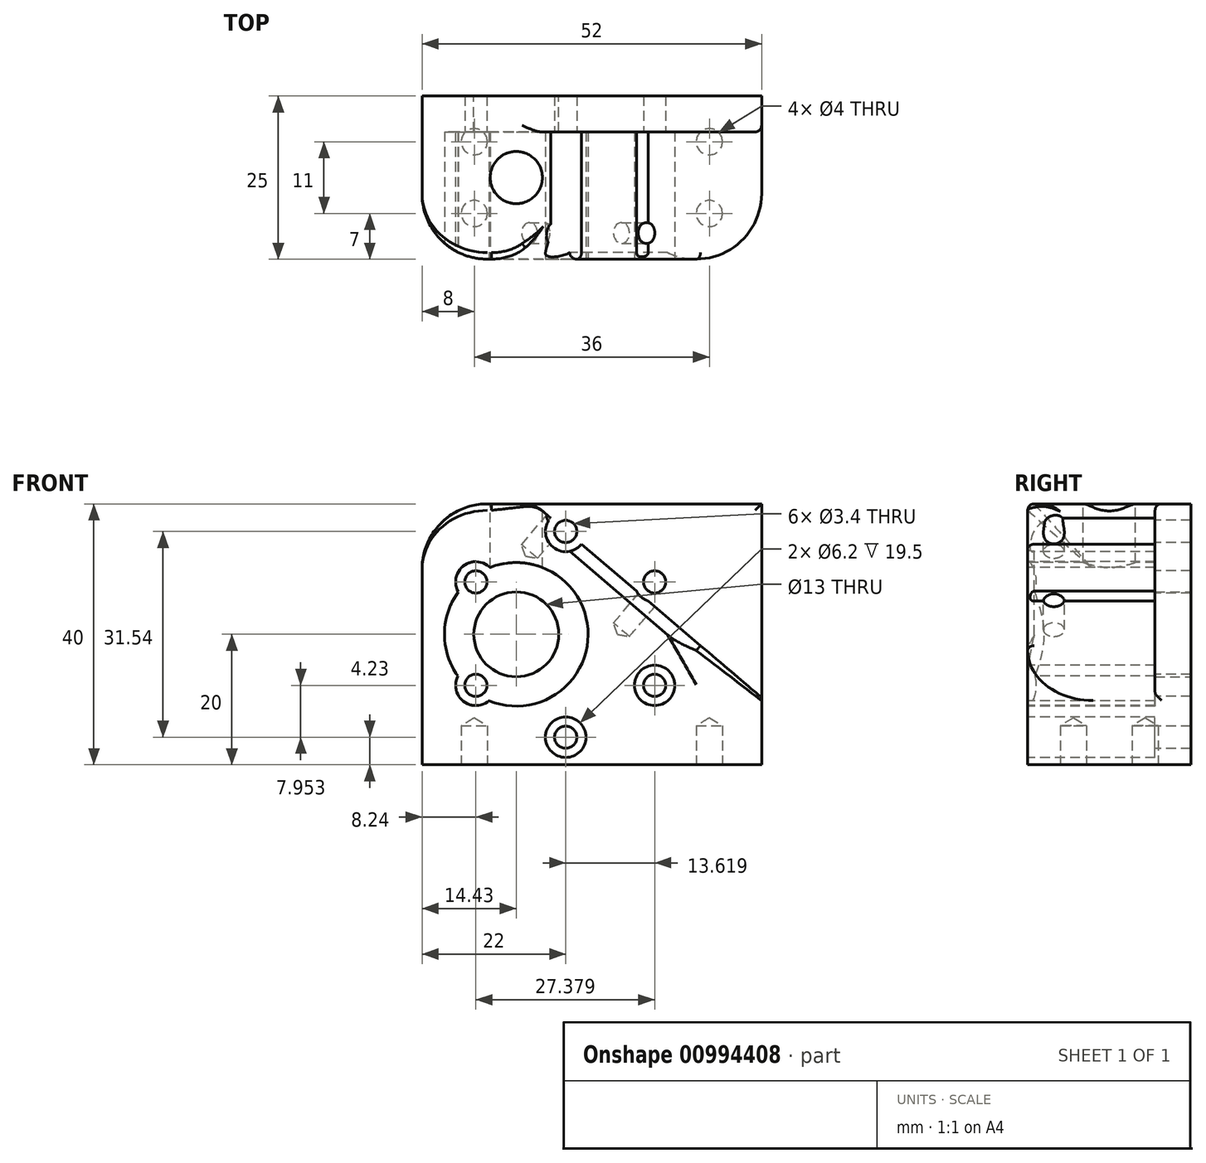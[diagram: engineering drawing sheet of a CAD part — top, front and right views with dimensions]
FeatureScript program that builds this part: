
annotation { "Feature Type Name" : "Feature", "Feature Type Description" : "" }
export const myFeature = defineFeature(function(context is Context, id is Id, definition is map)
    precondition{}
    {
        {
            var Q0;
            Q0=qCreatedBy(makeId("Front.planeOp"),FACE);
            var sketch = newSketch(context, id + "F0", { "sketchPlane" : qUnion([Q0])});
            skLineSegment(sketch, "E0.bottom", {"start": v(26, 20) * mm, "end": v(-26, 20) * mm});
            skLineSegment(sketch, "E0.top", {"start": v(26, -20) * mm, "end": v(-26, -20) * mm});
            skLineSegment(sketch, "E0.left", {"start": v(26, 20) * mm, "end": v(26, -20) * mm});
            skLineSegment(sketch, "E0.right", {"start": v(-26, 20) * mm, "end": v(-26, -20) * mm});
            skPoint(sketch, "E0.middle", {"position": v(0, 0) * mm});
            skLineSegment(sketch, "E1", {"start": v(-4, -15.77) * mm, "end": v(-4, 15.77) * mm});
            skPoint(sketch, "E2", {"position": v(9.66, -7.88) * mm});
            skPoint(sketch, "E3", {"position": v(9.66, 7.88) * mm});
            skPoint(sketch, "E4", {"position": v(11.77, 0) * mm});
            skPoint(sketch, "E5", {"position": v(-17.66, -7.88) * mm});
            skPoint(sketch, "E6", {"position": v(-17.66, 7.88) * mm});
            skCircle(sketch, "E7", {"center": v(-11.57, 0) * mm, "radius": 6.5 * mm});
            skPoint(sketch, "E8.center.orphan", {"position": v(-4, 0) * mm});
            skSolve(sketch);
        }
        {
            var Q0;
            Q0 = qSketchRegion(id + "F0", true);
            extrude(context, id + "F1", {"entities" : qUnion([Q0]), "endBound" : BoundingType.SYMMETRIC, "depth" : 25 * mm, "offsetDistance" : 25 * mm});
        }
        {
            var Q0;
            Q0=makeQuery(id+"F1.opExtrude","CAP_FACE",FACE,{"disambiguationData":[OSD([sQuery(id+"F0.wireOp",EDGE,"E0.bottom"),sQuery(id+"F0.wireOp",EDGE,"E0.top"),sQuery(id+"F0.wireOp",EDGE,"E0.left"),sQuery(id+"F0.wireOp",EDGE,"E0.right"),sQuery(id+"F0.wireOp",EDGE,"E7")])],"isStart":false});
            var sketch = newSketch(context, id + "F2", { "sketchPlane" : qUnion([Q0])});
            skPoint(sketch, "E9", {"position": v(-17.76, -7.82) * mm});
            skPoint(sketch, "E10", {"position": v(-17.76, 8.03) * mm});
            skPoint(sketch, "E11", {"position": v(9.62, -7.82) * mm});
            skPoint(sketch, "E12", {"position": v(9.62, 8.03) * mm});
            skPoint(sketch, "E13", {"position": v(-4, -15.77) * mm});
            skPoint(sketch, "E14", {"position": v(-4, 15.77) * mm});
            skSolve(sketch);
        }
        {
            var Q0;
            Q0=sQuery(id+"F2.wireOp",VERTEX,"E10");
            var Q1;
            Q1=sQuery(id+"F2.wireOp",VERTEX,"E14");
            var Q2;
            Q2=sQuery(id+"F2.wireOp",VERTEX,"E12");
            var Q3;
            Q3=sQuery(id+"F2.wireOp",VERTEX,"E11");
            var Q4;
            Q4=sQuery(id+"F2.wireOp",VERTEX,"E13");
            var Q5;
            Q5=sQuery(id+"F2.wireOp",VERTEX,"E9");
            var Q6;
            Q6=makeQuery(id+"F1.opExtrude","SWEPT_BODY",BODY,{"disambiguationData":[OSD([sQuery(id+"F0.wireOp",EDGE,"E0.bottom"),sQuery(id+"F0.wireOp",EDGE,"E0.top"),sQuery(id+"F0.wireOp",EDGE,"E0.left"),sQuery(id+"F0.wireOp",EDGE,"E0.right"),sQuery(id+"F0.wireOp",EDGE,"E7")])]});
            hole(context, id + "F3", {"style" : HoleStyle.C_BORE, "endStyle" : HoleEndStyle.THROUGH, "holeDiameter" : 3.4 * mm, "cBoreDiameter" : 6.2 * mm, "cBoreDepth" : 19.5 * mm, "majorDiameter" : 3 * mm, "isTappedThrough" : true, "tappedDepth" : 12 * mm, "tapClearance" : 3, "startFromSketch" : true, "locations" : qUnion([Q0, Q1, Q2, Q3, Q4, Q5]), "scope" : qUnion([Q6])});
        }
        {
            var Q0;
            Q0=makeQuery(id+"F2.imprint","IMPRINT",FACE,{"disambiguationData":[TD([[makeQuery(id+"F2.imprint","IMPRINT",EDGE,{"derivedFrom":makeQuery(id+"F1.opExtrude","CAP_EDGE",EDGE,{"disambiguationData":[OSD([sQuery(id+"F0.wireOp",EDGE,"E0.bottom")])],"isStart":false})}),1.0]])]});
            var sketch = newSketch(context, id + "F4", { "sketchPlane" : qUnion([Q0])});
            skCircle(sketch, "E15", {"center": v(-11.57, 0) * mm, "radius": 11 * mm});
            skSolve(sketch);
        }
        {
            var Q0;
            Q0 = qSketchRegion(id + "F4", true);
            extrude(context, id + "F5", {"entities" : qUnion([Q0]), "operationType" : NewBodyOperationType.REMOVE, "oppositeDirection" : true, "depth" : 19.5 * mm, "offsetDistance" : 25 * mm});
        }
        {
            var Q0;
            Q0=makeQuery(id+"F1.opExtrude","SWEPT_FACE",FACE,{"disambiguationData":[OSD([sQuery(id+"F0.wireOp",EDGE,"E0.bottom")])]});
            var sketch = newSketch(context, id + "F6", { "sketchPlane" : qUnion([Q0])});
            skPoint(sketch, "E16", {"position": v(-17.67, 0) * mm});
            skPoint(sketch, "E17", {"position": v(36.59, -1463.42) * mm});
            skPoint(sketch, "E18", {"position": v(-11.57, 0) * mm});
            skSolve(sketch);
        }
        {
            var Q0;
            Q0=sQuery(id+"F6.wireOp",VERTEX,"E18");
            var Q1;
            Q1=makeQuery(id+"F1.opExtrude","SWEPT_BODY",BODY,{"disambiguationData":[OSD([sQuery(id+"F0.wireOp",EDGE,"E0.bottom"),sQuery(id+"F0.wireOp",EDGE,"E0.top"),sQuery(id+"F0.wireOp",EDGE,"E0.left"),sQuery(id+"F0.wireOp",EDGE,"E0.right"),sQuery(id+"F0.wireOp",EDGE,"E7")])]});
            hole(context, id + "F7", {"style" : HoleStyle.SIMPLE, "endStyle" : HoleEndStyle.BLIND, "holeDiameter" : 8 * mm, "majorDiameter" : 5 * mm, "holeDepth" : 12 * mm, "isTappedThrough" : true, "tappedDepth" : 12 * mm, "tapClearance" : 3, "startFromSketch" : true, "locations" : qUnion([Q0]), "scope" : qUnion([Q1])});
        }
        {
            var Q0;
            Q0=makeQuery(id+"F1.opExtrude","SWEPT_FACE",FACE,{"disambiguationData":[OSD([sQuery(id+"F0.wireOp",EDGE,"E0.top")])]});
            var sketch = newSketch(context, id + "F8", { "sketchPlane" : qUnion([Q0])});
            skPoint(sketch, "E19", {"position": v(-18, 5.5) * mm});
            skPoint(sketch, "E20", {"position": v(18, 5.5) * mm});
            skPoint(sketch, "E21", {"position": v(18, -5.5) * mm});
            skPoint(sketch, "E22", {"position": v(-18, -5.5) * mm});
            skSolve(sketch);
        }
        {
            var Q0;
            Q0=sQuery(id+"F8.wireOp",VERTEX,"E19");
            var Q1;
            Q1=sQuery(id+"F8.wireOp",VERTEX,"E20");
            var Q2;
            Q2=sQuery(id+"F8.wireOp",VERTEX,"E22");
            var Q3;
            Q3=sQuery(id+"F8.wireOp",VERTEX,"E21");
            var Q4;
            Q4=makeQuery(id+"F1.opExtrude","SWEPT_BODY",BODY,{"disambiguationData":[OSD([sQuery(id+"F0.wireOp",EDGE,"E0.bottom"),sQuery(id+"F0.wireOp",EDGE,"E0.top"),sQuery(id+"F0.wireOp",EDGE,"E0.left"),sQuery(id+"F0.wireOp",EDGE,"E0.right"),sQuery(id+"F0.wireOp",EDGE,"E7")])]});
            hole(context, id + "F9", {"style" : HoleStyle.SIMPLE, "endStyle" : HoleEndStyle.BLIND, "holeDiameter" : 4 * mm, "majorDiameter" : 5 * mm, "holeDepth" : 6 * mm, "isTappedThrough" : true, "tappedDepth" : 12 * mm, "tapClearance" : 3, "startFromSketch" : true, "locations" : qUnion([Q0, Q1, Q2, Q3]), "scope" : qUnion([Q4])});
        }
        {
            var Q0;
            Q0=makeQuery(id+"F1.opExtrude","CAP_EDGE",EDGE,{"disambiguationData":[OSD([sQuery(id+"F0.wireOp",EDGE,"E0.right")])],"isStart":false});
            var Q1;
            Q1=makeQuery(id+"F1.opExtrude","CAP_EDGE",EDGE,{"disambiguationData":[OSD([sQuery(id+"F0.wireOp",EDGE,"E0.left")])],"isStart":false});
            fillet(context, id + "F10", {"entities" : qUnion([Q0, Q1]), "radius" : 10 * mm, "tangentPropagation" : true, "allowEdgeOverflow" : false});
        }
        {
            var Q0;
            Q0=makeQuery(id+"F1.opExtrude","CAP_FACE",FACE,{"disambiguationData":[OSD([sQuery(id+"F0.wireOp",EDGE,"E0.bottom"),sQuery(id+"F0.wireOp",EDGE,"E0.top"),sQuery(id+"F0.wireOp",EDGE,"E0.left"),sQuery(id+"F0.wireOp",EDGE,"E0.right"),sQuery(id+"F0.wireOp",EDGE,"E7")])],"isStart":false});
            var sketch = newSketch(context, id + "F11", { "sketchPlane" : qUnion([Q0])});
            skLineSegment(sketch, "E23", {"start": v(-9.05, 20.18) * mm, "end": v(26.15, -9.82) * mm});
            skLineSegment(sketch, "E24", {"start": v(26.15, -9.82) * mm, "end": v(26.15, 20.24) * mm});
            skLineSegment(sketch, "E25", {"start": v(26.15, 20.24) * mm, "end": v(-9.05, 20.18) * mm});
            skSolve(sketch);
        }
        {
            var Q0;
            Q0 = qSketchRegion(id + "F11", true);
            extrude(context, id + "F12", {"entities" : qUnion([Q0]), "operationType" : NewBodyOperationType.REMOVE, "oppositeDirection" : true, "depth" : 19.5 * mm, "offsetDistance" : 25 * mm});
        }
        {
            var Q0;
            Q0=makeQuery(id+"F1.opExtrude","CAP_EDGE",EDGE,{"disambiguationData":[OSD([sQuery(id+"F0.wireOp",EDGE,"E0.bottom")])],"isStart":false});
            fillet(context, id + "F13", {"entities" : qUnion([Q0]), "radius" : 10 * mm, "tangentPropagation" : true, "allowEdgeOverflow" : false});
        }
        {
            var Q0;
            Q0=makeQuery(id+"F12.boolean.opBoolean","INTERSECT",EDGE,{"derivedFrom":[makeQuery(id+"F1.opExtrude","SWEPT_FACE",FACE,{"disambiguationData":[OSD([sQuery(id+"F0.wireOp",EDGE,"E0.bottom")])]}),makeQuery(id+"F12.opExtrude","CAP_FACE",FACE,{"disambiguationData":[OSD([sQuery(id+"F11.wireOp",EDGE,"E23"),sQuery(id+"F11.wireOp",EDGE,"E24"),sQuery(id+"F11.wireOp",EDGE,"E25")])],"isStart":false})]});
            var Q1;
            Q1=makeQuery(id+"F12.boolean.opBoolean","INTERSECT",EDGE,{"derivedFrom":[makeQuery(id+"F1.opExtrude","SWEPT_FACE",FACE,{"disambiguationData":[OSD([sQuery(id+"F0.wireOp",EDGE,"E0.left")])]}),makeQuery(id+"F12.opExtrude","CAP_FACE",FACE,{"disambiguationData":[OSD([sQuery(id+"F11.wireOp",EDGE,"E23"),sQuery(id+"F11.wireOp",EDGE,"E24"),sQuery(id+"F11.wireOp",EDGE,"E25")])],"isStart":false})]});
            var Q2;
            Q2=makeQuery(id+"F12.boolean.opBoolean","INTERSECT",EDGE,{"derivedFrom":[makeQuery(id+"F1.opExtrude","SWEPT_FACE",FACE,{"disambiguationData":[OSD([sQuery(id+"F0.wireOp",EDGE,"E0.left")])]}),makeQuery(id+"F12.opExtrude","SWEPT_FACE",FACE,{"disambiguationData":[OSD([sQuery(id+"F11.wireOp",EDGE,"E23")])]})]});
            var Q3;
            {var subQ0=sQuery(id+"F0.wireOp",EDGE,"E0.bottom");var subQ1=sQuery(id+"F11.wireOp",EDGE,"E23");Q3=makeQuery(id+"F12.boolean.opBoolean","COPY",EDGE,{"disambiguationData":[TD([makeQuery(id+"F1.opExtrude","SWEPT_FACE",FACE,{"disambiguationData":[OSD([subQ0])]}),makeQuery(id+"F1.opExtrude","CAP_FACE",FACE,{"disambiguationData":[OSD([subQ0,sQuery(id+"F0.wireOp",EDGE,"E0.top"),sQuery(id+"F0.wireOp",EDGE,"E0.left"),sQuery(id+"F0.wireOp",EDGE,"E0.right"),sQuery(id+"F0.wireOp",EDGE,"E7")])],"isStart":false}),makeQuery(id+"F3.hole-1.boolean.opBoolean","COPY",FACE,{"derivedFrom":makeQuery(id+"F3.hole-1.opRevolve","SWEPT_FACE",FACE,{"disambiguationData":[OSD([sQuery(id+"F3.hole-1.sketch.wireOp",EDGE,"cbore_start_line_2")])]})}),makeQuery(id+"F12.opExtrude","SWEPT_FACE",FACE,{"disambiguationData":[OSD([subQ1])]})])],"derivedFrom":makeQuery(id+"F12.opExtrude","CAP_EDGE",EDGE,{"disambiguationData":[OSD([subQ1])],"isStart":true})});}
            var Q4;
            Q4=makeQuery(id+"F1.opExtrude","CAP_EDGE",EDGE,{"disambiguationData":[OSD([sQuery(id+"F0.wireOp",EDGE,"E0.bottom")])],"isStart":false});
            var Q5;
            Q5=makeQuery(id+"F12.boolean.opBoolean","INTERSECT",EDGE,{"derivedFrom":[makeQuery(id+"F10.opFillet","BLEND_FACE",FACE,{"disambiguationData":[OSD([sQuery(id+"F0.wireOp",EDGE,"E0.left")])]}),makeQuery(id+"F12.opExtrude","SWEPT_FACE",FACE,{"disambiguationData":[OSD([sQuery(id+"F11.wireOp",EDGE,"E23")])]})]});
            var Q6;
            {var subQ0=sQuery(id+"F0.wireOp",EDGE,"E0.left");var subQ1=sQuery(id+"F11.wireOp",EDGE,"E23");Q6=makeQuery(id+"F12.boolean.opBoolean","COPY",EDGE,{"disambiguationData":[TD([makeQuery(id+"F1.opExtrude","CAP_FACE",FACE,{"disambiguationData":[OSD([sQuery(id+"F0.wireOp",EDGE,"E0.bottom"),sQuery(id+"F0.wireOp",EDGE,"E0.top"),subQ0,sQuery(id+"F0.wireOp",EDGE,"E0.right"),sQuery(id+"F0.wireOp",EDGE,"E7")])],"isStart":false}),makeQuery(id+"F3.hole-2.boolean.opBoolean","COPY",FACE,{"derivedFrom":makeQuery(id+"F3.hole-2.opRevolve","SWEPT_FACE",FACE,{"disambiguationData":[OSD([sQuery(id+"F3.hole-2.sketch.wireOp",EDGE,"cbore_start_line_2")])]})}),makeQuery(id+"F10.opFillet","BLEND_FACE",FACE,{"disambiguationData":[OSD([subQ0])]}),makeQuery(id+"F12.opExtrude","SWEPT_FACE",FACE,{"disambiguationData":[OSD([subQ1])]})])],"derivedFrom":makeQuery(id+"F12.opExtrude","CAP_EDGE",EDGE,{"disambiguationData":[OSD([subQ1])],"isStart":true})});}
            var Q7;
            {var subQ0=sQuery(id+"F11.wireOp",EDGE,"E23");Q7=makeQuery(id+"F12.boolean.opBoolean","COPY",EDGE,{"disambiguationData":[TD([makeQuery(id+"F1.opExtrude","CAP_FACE",FACE,{"disambiguationData":[OSD([sQuery(id+"F0.wireOp",EDGE,"E0.bottom"),sQuery(id+"F0.wireOp",EDGE,"E0.top"),sQuery(id+"F0.wireOp",EDGE,"E0.left"),sQuery(id+"F0.wireOp",EDGE,"E0.right"),sQuery(id+"F0.wireOp",EDGE,"E7")])],"isStart":false}),makeQuery(id+"F3.hole-1.boolean.opBoolean","COPY",FACE,{"derivedFrom":makeQuery(id+"F3.hole-1.opRevolve","SWEPT_FACE",FACE,{"disambiguationData":[OSD([sQuery(id+"F3.hole-1.sketch.wireOp",EDGE,"cbore_start_line_2")])]})}),makeQuery(id+"F3.hole-2.boolean.opBoolean","COPY",FACE,{"derivedFrom":makeQuery(id+"F3.hole-2.opRevolve","SWEPT_FACE",FACE,{"disambiguationData":[OSD([sQuery(id+"F3.hole-2.sketch.wireOp",EDGE,"cbore_start_line_2")])]})}),makeQuery(id+"F12.opExtrude","SWEPT_FACE",FACE,{"disambiguationData":[OSD([subQ0])]})])],"derivedFrom":makeQuery(id+"F12.opExtrude","CAP_EDGE",EDGE,{"disambiguationData":[OSD([subQ0])],"isStart":true})});}
            fillet(context, id + "F14", {"entities" : qUnion([Q0, Q1, Q2, Q3, Q4, Q5, Q6, Q7]), "radius" : 1 * mm, "tangentPropagation" : true, "allowEdgeOverflow" : false});
        }
        {
            var Q0;
            {var subQ0=sQuery(id+"F11.wireOp",EDGE,"E23");Q0=makeQuery(id+"F12.boolean.opBoolean","COPY",FACE,{"disambiguationData":[TD([makeQuery(id+"F1.opExtrude","CAP_FACE",FACE,{"disambiguationData":[OSD([sQuery(id+"F0.wireOp",EDGE,"E0.bottom"),sQuery(id+"F0.wireOp",EDGE,"E0.top"),sQuery(id+"F0.wireOp",EDGE,"E0.left"),sQuery(id+"F0.wireOp",EDGE,"E0.right"),sQuery(id+"F0.wireOp",EDGE,"E7")])],"isStart":false}),makeQuery(id+"F3.hole-1.boolean.opBoolean","COPY",FACE,{"derivedFrom":makeQuery(id+"F3.hole-1.opRevolve","SWEPT_FACE",FACE,{"disambiguationData":[OSD([sQuery(id+"F3.hole-1.sketch.wireOp",EDGE,"cbore_start_line_1")])]})}),makeQuery(id+"F3.hole-1.boolean.opBoolean","COPY",FACE,{"derivedFrom":makeQuery(id+"F3.hole-1.opRevolve","SWEPT_FACE",FACE,{"disambiguationData":[OSD([sQuery(id+"F3.hole-1.sketch.wireOp",EDGE,"cbore_start_line_2")])]})}),makeQuery(id+"F3.hole-2.boolean.opBoolean","COPY",FACE,{"derivedFrom":makeQuery(id+"F3.hole-2.opRevolve","SWEPT_FACE",FACE,{"disambiguationData":[OSD([sQuery(id+"F3.hole-2.sketch.wireOp",EDGE,"cbore_start_line_1")])]})}),makeQuery(id+"F3.hole-2.boolean.opBoolean","COPY",FACE,{"derivedFrom":makeQuery(id+"F3.hole-2.opRevolve","SWEPT_FACE",FACE,{"disambiguationData":[OSD([sQuery(id+"F3.hole-2.sketch.wireOp",EDGE,"cbore_start_line_2")])]})}),makeQuery(id+"F12.opExtrude","CAP_FACE",FACE,{"disambiguationData":[OSD([subQ0,sQuery(id+"F11.wireOp",EDGE,"E24"),sQuery(id+"F11.wireOp",EDGE,"E25")])],"isStart":false})])],"derivedFrom":makeQuery(id+"F12.opExtrude","SWEPT_FACE",FACE,{"disambiguationData":[OSD([subQ0])]})});}
            var sketch = newSketch(context, id + "F15", { "sketchPlane" : qUnion([Q0])});
            skLineSegment(sketch, "E26.bottom", {"start": v(21.16, 4.62) * mm, "end": v(-18.5, 4.62) * mm});
            skLineSegment(sketch, "E26.top", {"start": v(21.16, -11.5) * mm, "end": v(-18.5, -11.5) * mm});
            skLineSegment(sketch, "E26.left", {"start": v(21.16, 4.62) * mm, "end": v(21.16, -11.5) * mm});
            skLineSegment(sketch, "E26.right", {"start": v(-18.5, 4.62) * mm, "end": v(-18.5, -11.5) * mm});
            skPoint(sketch, "E26.middle", {"position": v(1.33, -3.44) * mm});
            skPoint(sketch, "E27", {"position": v(-15.5, -8.5) * mm});
            skPoint(sketch, "E28", {"position": v(3, -8.5) * mm});
            skSolve(sketch);
        }
        {
            var Q0;
            Q0=sQuery(id+"F15.wireOp",VERTEX,"E27");
            var Q1;
            Q1=sQuery(id+"F15.wireOp",VERTEX,"E28");
            var Q2;
            Q2=makeQuery(id+"F1.opExtrude","SWEPT_BODY",BODY,{"disambiguationData":[OSD([sQuery(id+"F0.wireOp",EDGE,"E0.bottom"),sQuery(id+"F0.wireOp",EDGE,"E0.top"),sQuery(id+"F0.wireOp",EDGE,"E0.left"),sQuery(id+"F0.wireOp",EDGE,"E0.right"),sQuery(id+"F0.wireOp",EDGE,"E7")])]});
            hole(context, id + "F16", {"style" : HoleStyle.SIMPLE, "endStyle" : HoleEndStyle.BLIND, "standardTappedOrClearance" : lookupTablePath({ "fit" : "Close", "standard" : "ISO", "size" : "M3", "type" : "Clearance" }), "standardBlindInLast" : lookupTablePath({ "fit" : "Close", "standard" : "ISO", "engagement" : "75%", "pitch" : "0.5 mm", "size" : "M3", "type" : "Clearance & tapped" }), "holeDiameter" : 3.2 * mm, "majorDiameter" : 5 * mm, "holeDepth" : 6 * mm, "isTappedThrough" : true, "tappedDepth" : 12 * mm, "tapClearance" : 3, "startFromSketch" : true, "locations" : qUnion([Q0, Q1]), "scope" : qUnion([Q2])});
        }
        {
            var Q0;
            Q0=makeQuery(id+"F12.boolean.opBoolean","INTERSECT",EDGE,{"disambiguationData":[OD(0.0)],"derivedFrom":[makeQuery(id+"F1.opExtrude","SWEPT_FACE",FACE,{"disambiguationData":[OSD([sQuery(id+"F0.wireOp",EDGE,"E0.bottom")])]}),makeQuery(id+"F12.opExtrude","SWEPT_FACE",FACE,{"disambiguationData":[OSD([sQuery(id+"F11.wireOp",EDGE,"E23")])]})]});
            fillet(context, id + "F17", {"entities" : qUnion([Q0]), "radius" : 5 * mm, "tangentPropagation" : true, "allowEdgeOverflow" : false});
        }
    });
